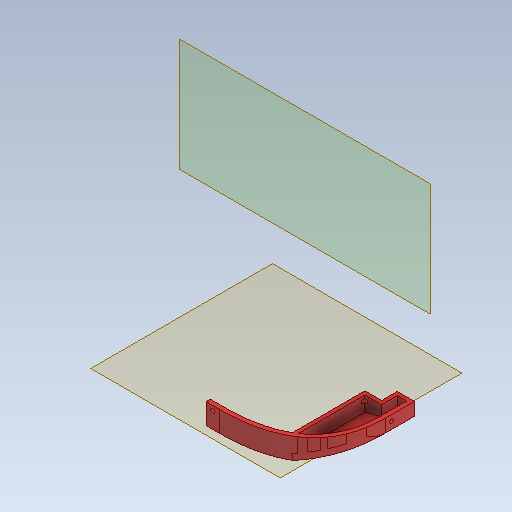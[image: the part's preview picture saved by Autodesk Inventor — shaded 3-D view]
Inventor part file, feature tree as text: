
AUTODESK INVENTOR PART (.ipt)
format: ipt  version: 2020 (Build 240168000, 168)  size: 349,184 bytes
history: native  units: mm
features: other x16, extrude x14, sketch x14
ambient origin geometry x8: Origin, YZ Plane, XZ Plane, XY Plane, X Axis, Y Axis, Z Axis, Center Point
bodies: Body1 (feature_tree)
feature tree (44):
  other  "Plano de trabalho1"
  extrude  "Extrusão6"  Depth=11.3mm TaperAngle=0.0deg
  extrude  "Extrusão7"  Depth=48.0mm TaperAngle=0.0deg
  extrude  "Extrusão8"  Depth=15.5mm TaperAngle=0.0deg
  extrude  "Extrusão9"  Depth=3.0mm
  extrude  "Extrusão10"  Depth=2.0mm
  extrude  "Extrusão11"  TaperAngle=0.0deg  [1 undecoded]
  extrude  "Extrusão12"  Depth=12.25mm TaperAngle=0.0deg
  extrude  "Extrusão13"  Depth=2.0mm
  extrude  "Extrusão14"  Depth=7.0mm
  extrude  "Extrusão15"  TaperAngle=0.0deg  [1 undecoded]
  extrude  "Extrusão16"  Depth=2.0mm TaperAngle=0.0deg
  sketch  "Esboço18"  dims[d63=7.0mm d64=11.3mm d65=0.0mm]
  extrude  "Extrusão18"  Depth=11.3mm TaperAngle=0.0deg
  extrude  "Extrusão19"  Depth=2.5mm
  other  "Plano de trabalho2"
  extrude  "Extrusão20"  Depth=4.25mm TaperAngle=0.0deg
  sketch  "Esboço7"  dims[d24=2.0mm d25=11.3mm d26=0.0mm]
  other  "Referência11"
  sketch  "Esboço8"  dims[d27=48.25mm d28=0.0mm d29=48.0mm d30=0.0mm]
  sketch  "Esboço9"  dims[d31=48.0mm d32=0.0mm d33=15.5mm d34=0.0mm]
  sketch  "Esboço10"  dims[d35=7.0mm d36=0.0mm d37=3.0mm]
  other  "Referência12"
  sketch  "Esboço11"  dims[d39=2.0mm d40=2.0mm]
  other  "Contorno projetado5"
  other  "Referência13"
  sketch  "Esboço12"  dims[d41=2.0mm d42=0.0mm]
  other  "Referência14"
  sketch  "Esboço13"  dims[d43=0.0mm d44=12.25mm d45=0.0mm]
  other  "Contorno projetado6"
  sketch  "Esboço14"  dims[d46=17.25mm d47=0.0mm d52=2.0mm]
  other  "Contorno projetado7"
  sketch  "Esboço15"  dims[d54=2.0mm d55=7.0mm]
  other  "Contorno projetado8"
  sketch  "Esboço16"  dims[d56=1.5mm d58=0.0mm]
  sketch  "Esboço17"  dims[d59=2.0mm d60=0.0mm d61=2.0mm d62=0.0mm]
  sketch  "Esboço20"  dims[d66=2.0mm d67=2.5mm]
  sketch  "Esboço21"  dims[d68=3.5mm d75=4.25mm d76=0.0mm d77=2.0mm d78=2.5mm d79=2.5mm d80=4.0mm d81=0.0mm d82=2.0mm d83=3.0mm d84=3.0mm d85=4.0mm d86=0.0mm d8=0.5mm d9=0.872665mm d10=0.5mm d11=0.872665mm d19=0.5mm d20=0.872665mm d21=0.5mm d22=0.872665mm d23=0.5mm]
  other  "<userpath>\Desktop\rabo\3d\ela.iam"
  other  "ela.iam"
  other  "lateral_V2:1"
  other  "frente:1"
  other  "PCB:1"
  other  "frente recurva:1"
note: 2 required parameter values undecoded (feature->parameter linkage not recoverable at this tier; creation-order binding heuristic only, values carry confidence <= 0.55)
